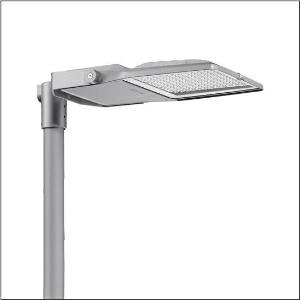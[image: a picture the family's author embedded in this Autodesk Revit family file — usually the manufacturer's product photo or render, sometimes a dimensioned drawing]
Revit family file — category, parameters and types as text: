
# Revit family: floodlight_fl_21_iq_midi___pl61_5xa7781f4c3a_8dc1
name_source: partatom
category: Lighting Fixtures
units: mm (PartAtom-declared; Revit-internal decimal feet)

## family parameters
Cut with Voids When Loaded = No
Host = Face
Light Source = No
Part Type = Normal
Room Calculation Point = No
Round Connector Dimension = Use Diameter
Shared = No

## types (1)
- --- (1 x LED, 36650 lm, 270.2 W, 4000K)
    Apparent Load = 270 VA
    CIE Flux Codes = 33 65 98 100 100
    Color Rendering = 70
    Color Temperature = 4000K
    Default Elevation = 1800 mm
    Description = Floodlight FL 21 iQ midi, floodlight, primary light control with lens, of PMMA, primary optical cover: protective disc, of toughened safety glass, transparent, light distribution: PL61, light emission: direct distribution, installation type: surface-mounted, lamps: LED, High Power LED, rated values: 36.650lm | 270,2W | 135,6lm/W (begin service life); end service life: 36.650lm | 286,6W; at 50% lumin. flux: 18.325lm | 117,7W | 155,7lm/W, colour temperature: 4000K, colour rendering: CRI > 70, light colour: 740, light setting 1 begin service life: 100% | 36.650lm | 270,2W | 135,6lm/W | 4.000K, light setting 1 end service life: 286,6W, further light settings possible, control: optimised constant luminous flux control (CLO 2.0), Desk-Remote (wireless, voltage-free reading and setting of iQ features in the workshop via application-optimized NFC function/RFID function), Light-Fading, Smart-Wire, Night-Set, Lumen-Switch, Temp-Guard, Auto-Match, pre-setting: linear dimming characteristic, with terminal, 6-pole, mains connection: 220..240V, AC, 50/60Hz, luminaire housing, of diecast aluminium, powder-coated, SITECO metallic grey (DB 702S), corrosivity category C5 mid according to DIN EN ISO 12944suitable for swimming poolschlorine-resistant, sealing non-destructively replaceable, please order mast flange separately, mast bracket, of steel, galvanised, powder-coated, SITECO metallic grey (DB 702S), protection rating (complete): IP66, insulation class (complete): insulation class II (safety insulation), certification: CE, ENEC, VDE, protection symbol: D, impact resistance: IK08, permissible operating ambient temperature: -40..+40°C, permissible operating ambient temperature for outdoor applications: -40..+50°C, standard: DIN EN 12944, LABS conformity tested according to VDMA 24364:2018-05, packaging unit: 1 piece

Light Distribution: PL61
    Height = 76 mm
    Lamp = 1 x LED
    Lamp Light Flux = 36650 lm
    Lamp Power = 270.2 W
    Lamp count = 1
    Length = 657 mm
    Luminous efficacy = 136 lm/W
    Manufacturer = Siteco
    ModVariant = No
    Model = 5XA7781F4C3A
    Mounting Place = Pole
    Mounting Type = Pole annexe
    Number of Poles = 1
    OnlyDefault = Yes
    Power Factor = 1
    Product Name = Floodlight FL 21 iQ midi | PL61
    Product group = floodlight | pylon annexe
    ProductGroupID = 6201
    Protection Class = Protection class II
    Protection Degree = IP 66
    RLX_Detail_Level = 1
    RLX_Emergency_Light_Flux = 0 lm
    RLX_Emergency_Type = 0
    RLX_Emergency_Type_DB = No
    RlxData = <blob elided: 154021 chars, md5=2bb0b3ff>
    Socket = socket
    Standby Power = 0 W
    System Light Flux = 36650 lm
    System Power = 270 W
    Type Comments = factory setting: luminous flux: 100 % | dim-lin: 254 | 620 mA
    Type Image = l_1007123.jpg
    URL = http://relux.com
    VarID = @adj_109913
    Voltage = 0 V
    Weight = 0.00 kg
    Width = 442 mm

## geometry (parser evidence)
native form markers: Blend x4, Sweep x13
no freeform markers — native parametric forms only
